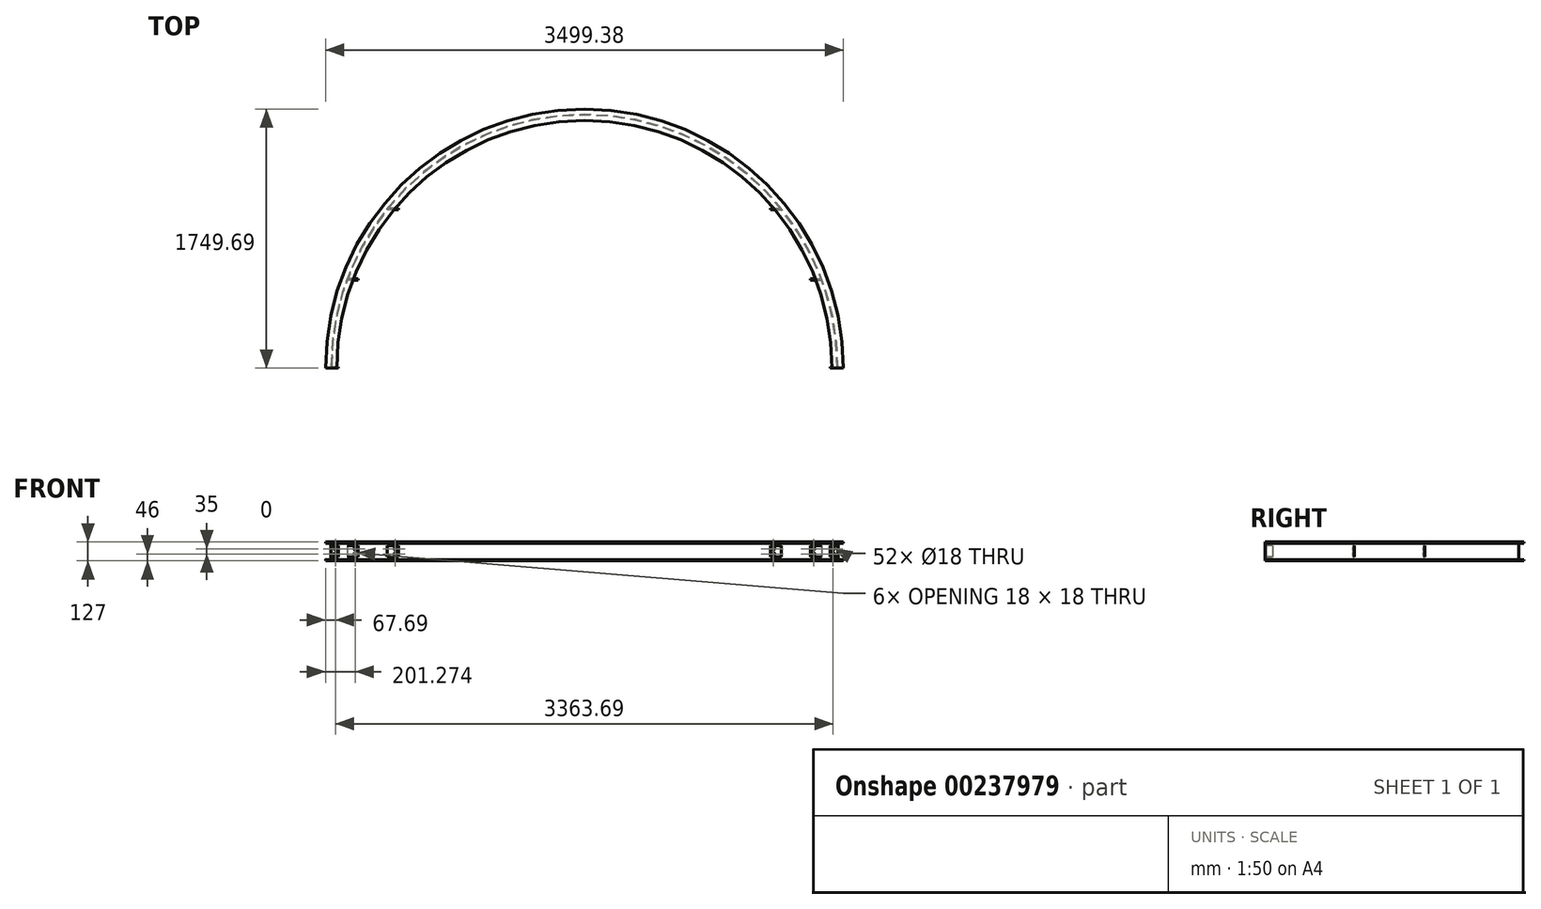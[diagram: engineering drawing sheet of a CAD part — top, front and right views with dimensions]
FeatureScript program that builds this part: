
annotation { "Feature Type Name" : "Feature", "Feature Type Description" : "" }
export const myFeature = defineFeature(function(context is Context, id is Id, definition is map)
    precondition{}
    {
        {
            var Q0;
            Q0=qCreatedBy(makeId("Front.planeOp"),FACE);
            var sketch = newSketch(context, id + "F0", { "sketchPlane" : qUnion([Q0])});
            skLineSegment(sketch, "E0", {"start": v(-37.7, 63.5) * mm, "end": v(38.3, 63.5) * mm});
            skLineSegment(sketch, "E1", {"start": v(38.3, 63.5) * mm, "end": v(38.3, 55.9) * mm});
            skLineSegment(sketch, "E2", {"start": v(38.3, 55.9) * mm, "end": v(2.3, 55.9) * mm});
            skLineSegment(sketch, "E3", {"start": v(2.3, 55.9) * mm, "end": v(2.3, -55.9) * mm});
            skLineSegment(sketch, "E4", {"start": v(2.3, -55.9) * mm, "end": v(38.3, -55.9) * mm});
            skLineSegment(sketch, "E5", {"start": v(38.3, -55.9) * mm, "end": v(38.3, -63.5) * mm});
            skLineSegment(sketch, "E6", {"start": v(38.3, -63.5) * mm, "end": v(-37.7, -63.5) * mm});
            skLineSegment(sketch, "E7", {"start": v(-37.7, -63.5) * mm, "end": v(-37.7, -55.9) * mm});
            skLineSegment(sketch, "E8", {"start": v(-37.7, -55.9) * mm, "end": v(-1.7, -55.9) * mm});
            skLineSegment(sketch, "E9", {"start": v(-1.7, -55.9) * mm, "end": v(-1.7, 55.9) * mm});
            skLineSegment(sketch, "E10", {"start": v(-1.7, 55.9) * mm, "end": v(-37.7, 55.9) * mm});
            skLineSegment(sketch, "E11", {"start": v(-37.7, 55.9) * mm, "end": v(-37.7, 63.5) * mm});
            skSolve(sketch);
        }
        {
            var Q0;
            Q0=qCreatedBy(makeId("Top.planeOp"),FACE);
            var sketch = newSketch(context, id + "F1", { "sketchPlane" : qUnion([Q0])});
            skArc(sketch, "E12", {"start": v(3424, 0) * mm, "mid": v(1712, 1712) * mm, "end": v(0, 0) * mm});
            skLineSegment(sketch, "E13", {"start": v(108.58, 600) * mm, "end": v(3315.42, 600) * mm});
            skLineSegment(sketch, "E14", {"start": v(379.59, 1075) * mm, "end": v(3044.41, 1075) * mm});
            skLineSegment(sketch, "E15", {"start": v(3038.89, 1081.85) * mm, "end": v(3051.44, 1066.28) * mm});
            skSolve(sketch);
        }
        {
            var Q0;
            Q0=makeQuery(id+"F0.imprint","IMPRINT",FACE,{"disambiguationData":[TD([[makeQuery(id+"F0.imprint","IMPRINT",EDGE,{"derivedFrom":sQuery(id+"F0.wireOp",EDGE,"E0")}),-1.0]])]});
            var Q1;
            Q1=sQuery(id+"F1.wireOp",EDGE,"E12");
            sweep(context, id + "F2", {"profiles" : qUnion([Q0]), "path" : qUnion([Q1])});
        }
        {
            var Q0;
            Q0=sQuery(id+"F1.wireOp",EDGE,"E14");
            var Q1;
            Q1=sQuery(id+"F1.wireOp",VERTEX,"E14.end");
            cPlane(context, id + "F3", {"entities" : qUnion([Q0, Q1]), "cplaneType" : CPlaneType.CURVE_POINT, "offset" : 25 * mm, "flipAlignment" : true, "width" : 150 * mm, "height" : 150 * mm});
        }
        {
            var Q0;
            Q0=sQuery(id+"F1.wireOp",VERTEX,"E13.end");
            var Q1;
            Q1=sQuery(id+"F1.wireOp",EDGE,"E13");
            cPlane(context, id + "F4", {"entities" : qUnion([Q0, Q1]), "cplaneType" : CPlaneType.CURVE_POINT, "offset" : 25 * mm, "width" : 150 * mm, "height" : 150 * mm});
        }
        {
            var Q0;
            Q0=qCreatedBy(id+"F3.planeOp",FACE);
            var sketch = newSketch(context, id + "F5", { "sketchPlane" : qUnion([Q0])});
            skLineSegment(sketch, "E16.bottom", {"start": v(1069.6, 37.5) * mm, "end": v(1079.6, 37.5) * mm});
            skLineSegment(sketch, "E16.top", {"start": v(1069.6, -37.5) * mm, "end": v(1079.6, -37.5) * mm});
            skLineSegment(sketch, "E16.left", {"start": v(1069.6, 37.5) * mm, "end": v(1069.6, -37.5) * mm});
            skLineSegment(sketch, "E16.right", {"start": v(1079.6, 37.5) * mm, "end": v(1079.6, -37.5) * mm});
            skSolve(sketch);
        }
        {
            var Q0;
            Q0=qSketchRegion(id+"F5",true);
            extrude(context, id + "F6", {"entities" : qUnion([Q0]), "oppositeDirection" : true, "depth" : 75 * mm});
        }
        {
            var Q0;
            Q0=sQuery(id+"F1.wireOp",EDGE,"E13");
            var Q1;
            Q1=sQuery(id+"F1.wireOp",VERTEX,"E13.start");
            cPlane(context, id + "F7", {"entities" : qUnion([Q0, Q1]), "cplaneType" : CPlaneType.CURVE_POINT, "offset" : 25 * mm, "width" : 150 * mm, "height" : 150 * mm});
        }
        {
            var Q0;
            Q0=sQuery(id+"F1.wireOp",EDGE,"E14");
            var Q1;
            Q1=sQuery(id+"F1.wireOp",VERTEX,"E14.start");
            cPlane(context, id + "F8", {"entities" : qUnion([Q0, Q1]), "cplaneType" : CPlaneType.CURVE_POINT, "offset" : 25 * mm, "width" : 150 * mm, "height" : 150 * mm});
        }
        {
            var Q0;
            Q0=qCreatedBy(id+"F7.planeOp",FACE);
            var sketch = newSketch(context, id + "F9", { "sketchPlane" : qUnion([Q0])});
            skLineSegment(sketch, "E17.bottom", {"start": v(605, 37.5) * mm, "end": v(595, 37.5) * mm});
            skLineSegment(sketch, "E17.top", {"start": v(605, -37.5) * mm, "end": v(595, -37.5) * mm});
            skLineSegment(sketch, "E17.left", {"start": v(605, 37.5) * mm, "end": v(605, -37.5) * mm});
            skLineSegment(sketch, "E17.right", {"start": v(595, 37.5) * mm, "end": v(595, -37.5) * mm});
            skSolve(sketch);
        }
        {
            var Q0;
            Q0=makeQuery(id+"F9.imprint","IMPRINT",FACE,{"disambiguationData":[TD([[makeQuery(id+"F9.imprint","IMPRINT",EDGE,{"derivedFrom":sQuery(id+"F9.wireOp",EDGE,"E17.bottom")}),1.0]])]});
            extrude(context, id + "F10", {"entities" : qUnion([Q0]), "depth" : 75 * mm});
        }
        {
            var Q0;
            Q0=qCreatedBy(id+"F4.planeOp",FACE);
            var sketch = newSketch(context, id + "F11", { "sketchPlane" : qUnion([Q0])});
            skLineSegment(sketch, "E18.bottom", {"start": v(594.81, 37.5) * mm, "end": v(604.81, 37.5) * mm});
            skLineSegment(sketch, "E18.top", {"start": v(594.81, -37.5) * mm, "end": v(604.81, -37.5) * mm});
            skLineSegment(sketch, "E18.left", {"start": v(594.81, 37.5) * mm, "end": v(594.81, -37.5) * mm});
            skLineSegment(sketch, "E18.right", {"start": v(604.81, 37.5) * mm, "end": v(604.81, -37.5) * mm});
            skSolve(sketch);
        }
        {
            var Q0;
            Q0=makeQuery(id+"F11.imprint","IMPRINT",FACE,{"disambiguationData":[TD([[makeQuery(id+"F11.imprint","IMPRINT",EDGE,{"derivedFrom":sQuery(id+"F11.wireOp",EDGE,"E18.bottom")}),-1.0]])]});
            extrude(context, id + "F12", {"entities" : qUnion([Q0]), "oppositeDirection" : true, "depth" : 75 * mm});
        }
        {
            var Q0;
            Q0=qCreatedBy(id+"F8.planeOp",FACE);
            var sketch = newSketch(context, id + "F13", { "sketchPlane" : qUnion([Q0])});
            skLineSegment(sketch, "E19.bottom", {"start": v(1069.97, 37.5) * mm, "end": v(1079.97, 37.5) * mm});
            skLineSegment(sketch, "E19.top", {"start": v(1069.97, -37.5) * mm, "end": v(1079.97, -37.5) * mm});
            skLineSegment(sketch, "E19.left", {"start": v(1069.97, 37.5) * mm, "end": v(1069.97, -37.5) * mm});
            skLineSegment(sketch, "E19.right", {"start": v(1079.97, 37.5) * mm, "end": v(1079.97, -37.5) * mm});
            skSolve(sketch);
        }
        {
            var Q0;
            Q0=makeQuery(id+"F13.imprint","IMPRINT",FACE,{"disambiguationData":[TD([[makeQuery(id+"F13.imprint","IMPRINT",EDGE,{"derivedFrom":sQuery(id+"F13.wireOp",EDGE,"E19.bottom")}),-1.0]])]});
            extrude(context, id + "F14", {"entities" : qUnion([Q0]), "depth" : 75 * mm});
        }
        {
            var Q0;
            Q0=makeQuery(id+"F14.opExtrude","SWEPT_FACE",FACE,{"disambiguationData":[OSD([sQuery(id+"F13.wireOp",EDGE,"E19.left")])]});
            var sketch = newSketch(context, id + "F15", { "sketchPlane" : qUnion([Q0])});
            skCircle(sketch, "E20", {"center": v(434.59, 17.5) * mm, "radius": 9 * mm});
            skPoint(sketch, "E20.centerSnap0", {"position": v(434.59, 37.5) * mm});
            skCircle(sketch, "E21", {"center": v(434.59, -17.5) * mm, "radius": 9 * mm});
            skSolve(sketch);
        }
        {
            var Q0;
            Q0=qSketchRegion(id+"F15",true);
            extrude(context, id + "F16", {"entities" : qUnion([Q0]), "operationType" : NewBodyOperationType.REMOVE, "oppositeDirection" : true, "depth" : 10 * mm});
        }
        {
            var Q0;
            Q0=makeQuery(id+"F10.opExtrude","SWEPT_FACE",FACE,{"disambiguationData":[OSD([sQuery(id+"F9.wireOp",EDGE,"E17.right")])]});
            var sketch = newSketch(context, id + "F17", { "sketchPlane" : qUnion([Q0])});
            skCircle(sketch, "E22", {"center": v(163.58, 17.5) * mm, "radius": 9 * mm});
            skCircle(sketch, "E23", {"center": v(163.58, -17.5) * mm, "radius": 9 * mm});
            skSolve(sketch);
        }
        {
            var Q0;
            Q0=qSketchRegion(id+"F17",true);
            extrude(context, id + "F18", {"entities" : qUnion([Q0]), "operationType" : NewBodyOperationType.REMOVE, "oppositeDirection" : true, "depth" : 25 * mm});
        }
        {
            var Q0;
            Q0=makeQuery(id+"F12.opExtrude","SWEPT_FACE",FACE,{"disambiguationData":[OSD([sQuery(id+"F11.wireOp",EDGE,"E18.left")])]});
            var sketch = newSketch(context, id + "F19", { "sketchPlane" : qUnion([Q0])});
            skCircle(sketch, "E24", {"center": v(3260.42, 17.5) * mm, "radius": 9 * mm});
            skCircle(sketch, "E25", {"center": v(3260.42, -17.5) * mm, "radius": 9 * mm});
            skSolve(sketch);
        }
        {
            var Q0;
            Q0=qSketchRegion(id+"F19",true);
            extrude(context, id + "F20", {"entities" : qUnion([Q0]), "operationType" : NewBodyOperationType.REMOVE, "oppositeDirection" : true, "depth" : 25 * mm});
        }
        {
            var Q0;
            Q0=makeQuery(id+"F6.opExtrude","SWEPT_FACE",FACE,{"disambiguationData":[OSD([sQuery(id+"F5.wireOp",EDGE,"E16.left")])]});
            var sketch = newSketch(context, id + "F21", { "sketchPlane" : qUnion([Q0])});
            skCircle(sketch, "E26", {"center": v(2989.41, 17.5) * mm, "radius": 9 * mm});
            skCircle(sketch, "E27", {"center": v(2989.41, -17.5) * mm, "radius": 9 * mm});
            skSolve(sketch);
        }
        {
            var Q0;
            Q0=qSketchRegion(id+"F21",true);
            extrude(context, id + "F22", {"entities" : qUnion([Q0]), "operationType" : NewBodyOperationType.REMOVE, "oppositeDirection" : true, "depth" : 25 * mm});
        }
        {
            var Q0;
            Q0=qCreatedBy(makeId("Top.planeOp"),FACE);
            var sketch = newSketch(context, id + "F23", { "sketchPlane" : qUnion([Q0])});
            skLineSegment(sketch, "E28.bottom", {"start": v(0, 50) * mm, "end": v(6, 50) * mm});
            skLineSegment(sketch, "E28.top", {"start": v(0, 0) * mm, "end": v(6, 0) * mm});
            skLineSegment(sketch, "E28.left", {"start": v(0, 50) * mm, "end": v(0, 0) * mm});
            skLineSegment(sketch, "E28.right", {"start": v(6, 50) * mm, "end": v(6, 6) * mm});
            skLineSegment(sketch, "E29.bottom", {"start": v(6, 6) * mm, "end": v(50, 6) * mm});
            skLineSegment(sketch, "E29.top", {"start": v(6, 0) * mm, "end": v(50, 0) * mm});
            skLineSegment(sketch, "E29.right", {"start": v(50, 6) * mm, "end": v(50, 0) * mm});
            skLineSegment(sketch, "E30.bottom", {"start": v(3423.7, 50) * mm, "end": v(3417.7, 50) * mm});
            skLineSegment(sketch, "E30.top", {"start": v(3423.7, 0) * mm, "end": v(3417.7, 0) * mm});
            skLineSegment(sketch, "E30.left", {"start": v(3423.7, 50) * mm, "end": v(3423.7, 0) * mm});
            skLineSegment(sketch, "E30.right", {"start": v(3417.7, 50) * mm, "end": v(3417.7, 6) * mm});
            skLineSegment(sketch, "E31.bottom", {"start": v(3373.7, 6) * mm, "end": v(3417.7, 6) * mm});
            skLineSegment(sketch, "E31.top", {"start": v(3373.7, 0) * mm, "end": v(3423.7, 0) * mm});
            skLineSegment(sketch, "E31.left", {"start": v(3373.7, 6) * mm, "end": v(3373.7, 0) * mm});
            skLineSegment(sketch, "E31.right", {"start": v(3423.7, 6) * mm, "end": v(3423.7, 0) * mm});
            skSolve(sketch);
        }
        {
            var Q0;
            Q0=makeQuery(id+"F23.imprint","IMPRINT",FACE,{"disambiguationData":[TD([[makeQuery(id+"F23.imprint","IMPRINT",EDGE,{"derivedFrom":sQuery(id+"F23.wireOp",EDGE,"E30.bottom")}),1.0]])]});
            var Q1;
            Q1=makeQuery(id+"F23.imprint","IMPRINT",FACE,{"disambiguationData":[TD([[makeQuery(id+"F23.imprint","IMPRINT",EDGE,{"derivedFrom":sQuery(id+"F23.wireOp",EDGE,"E28.bottom")}),-1.0]])]});
            extrude(context, id + "F24", {"entities" : qUnion([Q0, Q1]), "operationType" : NewBodyOperationType.ADD, "endBound" : BoundingType.SYMMETRIC, "depth" : 75 * mm});
        }
        {
            var Q0;
            Q0=qCreatedBy(makeId("Front.planeOp"),FACE);
            var sketch = newSketch(context, id + "F25", { "sketchPlane" : qUnion([Q0])});
            skCircle(sketch, "E32", {"center": v(30, 17.5) * mm, "radius": 9 * mm});
            skCircle(sketch, "E33", {"center": v(30, -17.5) * mm, "radius": 9 * mm});
            skCircle(sketch, "E34", {"center": v(3393.7, 17.5) * mm, "radius": 9 * mm});
            skCircle(sketch, "E35", {"center": v(3393.7, -17.5) * mm, "radius": 9 * mm});
            skSolve(sketch);
        }
        {
            var Q0;
            Q0 = qSketchRegion(id + "F25", true);
            extrude(context, id + "F26", {"entities" : qUnion([Q0]), "operationType" : NewBodyOperationType.REMOVE, "oppositeDirection" : true, "depth" : 25 * mm});
        }
    });
